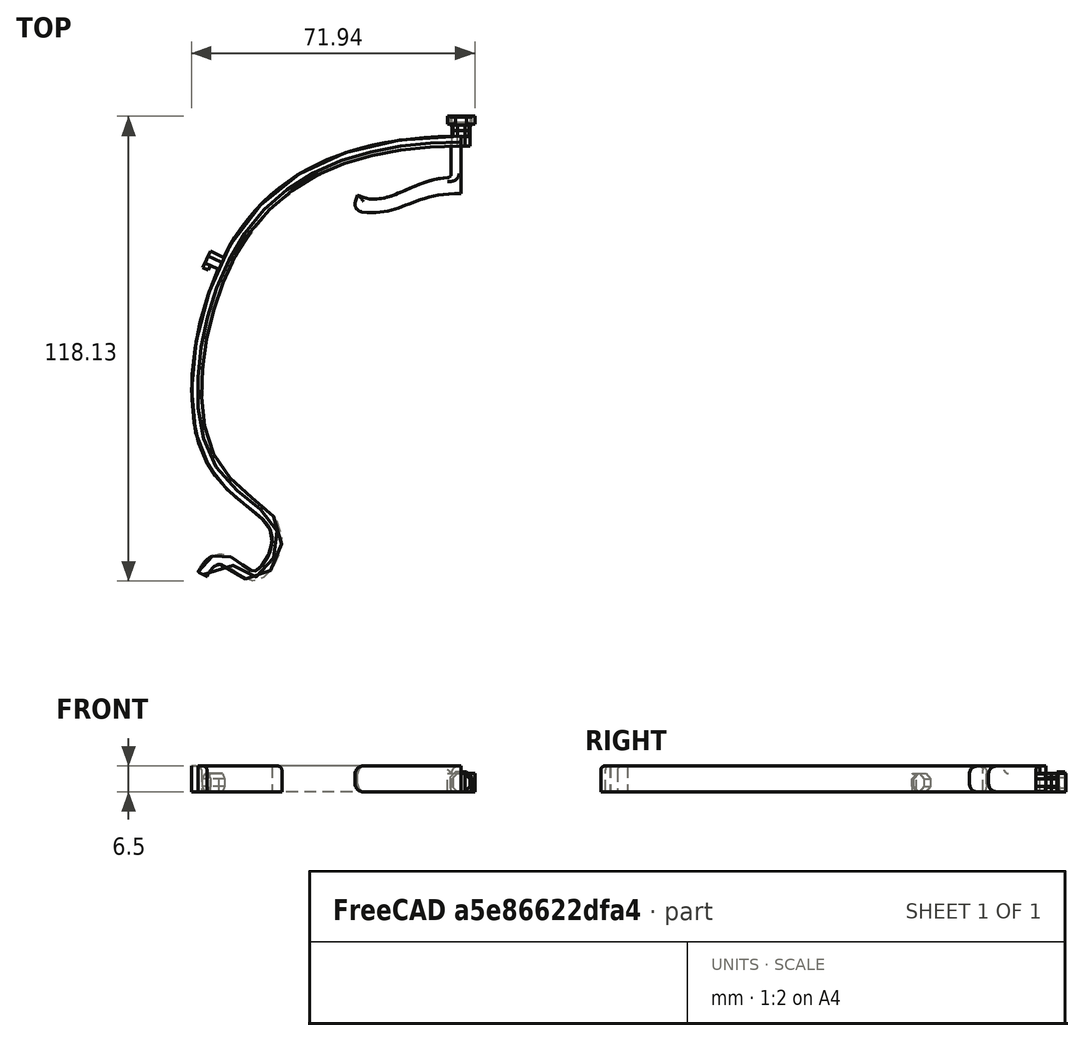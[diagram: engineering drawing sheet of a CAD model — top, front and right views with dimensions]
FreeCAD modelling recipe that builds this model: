
FCSTD DOCUMENT  (FreeCAD 0.18R16146 (Git))
Label: frame-001-03
License: All rights reserved
LicenseURL: http://ja.wikipedia.org/wiki/%E8%91%97%E4%BD%9C%E6%A8%A9%E8%A1%A8%E7%A4%BA
objects: Sketcher::SketchObject×5, Part::Extrusion×5, Part::Box×3, Part::Cut×2, Part::Fillet×2, Part::Compound×2, Mesh::Feature×1, Part::Sweep×1, Part::Mirroring×1, Part::MultiCommon×1
note: 22 computed .brp shape members not serialized (recipe doc carries the construction recipe); baked Part::Feature solids carry a one-line shape summary decoded from their .brp

FEATURE [Sketcher::SketchObject] Sketch  label="Sketch_FrameShape"
  sketch-geometry (15):
    g0-g7: Circle [constr] x8 (B-spline internal-alignment scaffolding for g8; pole/knot coordinates omitted)
    g8: BSplineCurve PolesCount=8 KnotsCount=6 Degree=3 IsPeriodic=0
    g9-g14: GeomPoint [constr] x6 (B-spline internal-alignment scaffolding for g8; pole/knot coordinates omitted)
  constraints (6):
    c: Radius(g0) = 6
    c: Equal(g0, g1-g6) x6
    c: InternalAlignment(g0-g7 -> g8) x8
    c: InternalAlignment(g9-g14 -> g8) x6
    c: Horizontal(g1,g8)
    c: Coincident(g-1,g8)
FEATURE [Sketcher::SketchObject] Sketch001
  Placement = pos=(0,0,0) rot=(0.57735,0.57735,0.57735;2.0944rad)
  sketch-geometry (4):
    g0: LineSegment StartX=0 StartY=6.5 StartZ=0 EndX=2.5 EndY=6.5 EndZ=0
    g1: LineSegment StartX=2.5 StartY=6.5 StartZ=0 EndX=2.5 EndY=0 EndZ=0
    g2: LineSegment StartX=2.5 StartY=0 StartZ=0 EndX=0 EndY=0 EndZ=0
    g3: LineSegment StartX=0 StartY=0 StartZ=0 EndX=0 EndY=6.5 EndZ=0
  constraints (12):
    c: Coincident(g0,g1)
    c: Coincident(g1,g2)
    c: Coincident(g2,g3)
    c: Coincident(g3,g0)
    c: Horizontal(g0)
    c: Horizontal(g2)
    c: Vertical(g1)
    c: Vertical(g3)
    c: DistanceX(g0,g0) = 2.5
    c: DistanceY(g1,g0) = 6.5
    c: DistanceX(g-1,g2) = 0
    c: PointOnObject(g2,g-1)
FEATURE [Mesh::Feature] cd43cbcc_75a4_11ea_893f_42010a00001e_UM3E_Visor_frame_EUROPE_ISO838_v3  label="cd43cbcc-75a4-11ea-893f-42010a00001e_UM3E_Visor_frame_EUROPE_ISO838_v3"
  Placement = pos=(0,-59,0) rot=(0,0,1;0rad)
FEATURE [Sketcher::SketchObject] Sketch002  label="OctPinSketch"
  Placement = pos=(0,0,0) rot=(1,0,0;1.5708rad)
  sketch-geometry (9):
    g0: LineSegment StartX=2.3097 StartY=1.35299 StartZ=0 EndX=2.3097 EndY=3.26641 EndZ=0
    g1: LineSegment StartX=2.3097 StartY=3.26641 StartZ=0 EndX=0.956709 EndY=4.6194 EndZ=0
    g2: LineSegment StartX=0.956709 StartY=4.6194 StartZ=0 EndX=-0.956709 EndY=4.6194 EndZ=0
    g3: LineSegment StartX=-0.956709 StartY=4.6194 StartZ=0 EndX=-2.3097 EndY=3.26641 EndZ=0
    g4: LineSegment StartX=-2.3097 StartY=3.26641 StartZ=0 EndX=-2.3097 EndY=1.35299 EndZ=0
    g5: LineSegment StartX=-2.3097 StartY=1.35299 StartZ=0 EndX=-0.956709 EndY=0 EndZ=0
    g6: LineSegment StartX=-0.956709 StartY=0 StartZ=0 EndX=0.956709 EndY=0 EndZ=0
    g7: LineSegment StartX=0.956709 StartY=0 StartZ=0 EndX=2.3097 EndY=1.35299 EndZ=0
    g8: Circle [constr] CenterX=0 CenterY=2.3097 CenterZ=0 NormalX=0 NormalY=0 NormalZ=1 AngleXU=0 Radius=2.5
  constraints (21):
    c: Coincident(g0,g1)
    c: Coincident(g1,g2)
    c: Coincident(g2,g3)
    c: Coincident(g3,g4)
    c: Coincident(g4,g5)
    c: Coincident(g5,g6)
    c: Coincident(g6,g7)
    c: Coincident(g7,g0)
    c: Equal(g0, g1-g7) x7
    c: PointOnObject(g0,g8)
    c: PointOnObject(g1,g8)
    c: PointOnObject(g2,g8)
    c: PointOnObject(g3,g8)
    c: PointOnObject(g4,g8)
    c: PointOnObject(g5,g8)
    c: PointOnObject(g6,g8)
    c: PointOnObject(g7,g8)
    c: Distance(g0,g8) = 2.5
    c: Horizontal(g6)
    c: PointOnObject(g8,g-2)
    c: PointOnObject(g6,g-1)
FEATURE [Part::Extrusion] Extrude002  label="OctPin"
  Base = -> Sketch002
  Dir = (0,-1,0)
  DirMode = 2
  FaceMakerClass = Part::FaceMakerBullseye
  LengthFwd = -6
  LengthRev = 0
  Solid = true
  Symmetric = false
FEATURE [Part::Extrusion] Extrude003  label="OctPinFront"
  Base = -> Sketch002
  Dir = (0,-1,2e-16)
  DirMode = 2
  FaceMakerClass = Part::FaceMakerBullseye
  LengthFwd = -3
  LengthRev = 0
  Placement = pos=(0,3,0) rot=(0,0,1;0rad)
  Solid = true
  Symmetric = false
FEATURE [Part::Extrusion] Extrude004  label="OctPin_WNotch_column"
  Base = -> Sketch002
  Dir = (0,-1,2e-16)
  DirMode = 2
  FaceMakerClass = Part::FaceMakerBullseye
  LengthFwd = -4
  LengthRev = 0
  Solid = true
  Symmetric = false
FEATURE [Part::Box] Box008  label="立方体008"
  AttacherType = Attacher::AttachEngine3D
  Height = 6
  Length = 2
  Placement = pos=(1,0,-0.5) rot=(0,0,1;0rad)
  Width = 2.5
FEATURE [Part::Cut] Cut  label="OctPin_WNotch"
  Base = -> Extrude004
  Tool = -> Box008
FEATURE [Part::Cut] Cut001  label="OctPin_WNotchR"
  Base = -> Extrude004
  Placement = pos=(61,-30.51,0) rot=(0,0,-1;1.13446rad)
  Tool = -> Box008
FEATURE [Sketcher::SketchObject] Sketch003
  sketch-geometry (18):
    g0: LineSegment StartX=0 StartY=1 StartZ=0 EndX=0 EndY=-12 EndZ=0
    g1: LineSegment StartX=2.5 StartY=-8 StartZ=0 EndX=2.5 EndY=1 EndZ=0
    g2: LineSegment StartX=2.5 StartY=1 StartZ=0 EndX=0 EndY=1 EndZ=0
    g3: LineSegment StartX=26.2521 StartY=-12.5 StartZ=0 EndX=27.6498 EndY=-16.2478 EndZ=0
    g4-g7: Circle [constr] x4 (B-spline internal-alignment scaffolding for g8; pole/knot coordinates omitted)
    g8: BSplineCurve PolesCount=4 KnotsCount=2 Degree=3 IsPeriodic=0
    g9: GeomPoint [constr] X=2.5 Y=-8 Z=0
    g10: GeomPoint [constr] X=26.2521 Y=-12.5 Z=0
    g11-g14: Circle [constr] x4 (B-spline internal-alignment scaffolding for g15; pole/knot coordinates omitted)
    g15: BSplineCurve PolesCount=4 KnotsCount=2 Degree=3 IsPeriodic=0
    g16: GeomPoint [constr] X=0 Y=-12 Z=0
    g17: GeomPoint [constr] X=27.6498 Y=-16.2478 Z=0
  constraints (32):
    c: PointOnObject(g0,g-2)
    c: Vertical(g0)
    c: Vertical(g1)
    c: Coincident(g1,g2)
    c: Coincident(g2,g0)
    c: DistanceX(g0,g1) = 2.5
    c: Horizontal(g2)
    c: DistanceY(g-1,g0) = 1
    c: DistanceY(g3,g1) = 4.5
    c: DistanceY(g0,g1) = 4
    c: DistanceY(g0,g-1) = 12
    c: Coincident(g8,g1)
    c: Radius(g4) = 2
    c: Equal(g4,g5)
    c: Equal(g4,g6)
    c: Equal(g4,g7)
    c: Coincident(g8,g3)
    c: InternalAlignment(g4-g7 -> g8) x4
    c: InternalAlignment(g9,g8)
    c: InternalAlignment(g10,g8)
    c: Coincident(g15,g0)
    c: Radius(g11) = 2
    c: Equal(g11,g12)
    c: Equal(g11,g13)
    c: Equal(g11,g14)
    c: Coincident(g15,g3)
    c: InternalAlignment(g11-g14 -> g15) x4
    c: InternalAlignment(g16,g15)
    c: InternalAlignment(g17,g15)
    c: Distance(g3,g3) = 4
    c: Horizontal(g0,g12)
    c: Horizontal(g5,g1)
FEATURE [Part::Extrusion] Extrude
  Base = -> Sketch003
  Dir = (0,0,1)
  DirMode = 2
  FaceMakerClass = Part::FaceMakerBullseye
  LengthFwd = 6.5
  LengthRev = 0
  Solid = true
  Symmetric = false
FEATURE [Part::Fillet] Fillet  label="AGOATE_R"
  Base = -> Extrude
  Edges = 8 edges: [Edge1 r=1,Edge4 r=2,Edge11 r=2,Edge12 r=2,Edge13 r=2,Edge15 r=2,Edge16 r=2,Edge18 r=1]
FEATURE [Part::Sweep] Sweep  label="Sweep_RightFrame"
  Frenet = false
  Sections = -> [Sketch001]
  Solid = true
  Spine = -> Sketch [Edge1]
  Transition = 1
FEATURE [Part::Fillet] Fillet001  label="Fillet_Sweep_RightFrame"
  Base = -> Sweep
  Edges = 1 edges r=1: [Edge1]
FEATURE [Part::Compound] Compound  label="RightSide"
  Links = -> [Cut001,Fillet,Fillet001]
FEATURE [Part::Mirroring] Part__Mirroring001  label="LeftSide (Mirrored)"
  Base = (2.38419e-07,-54.0124,3.5)
  Normal = (1,0,-1.19209e-07)
  Source = -> Compound
FEATURE [Part::Box] Box  label="立方体"
  AttacherType = Attacher::AttachEngine3D
  Height = 10
  Length = 4
  Placement = pos=(-2,2.8,0) rot=(0,0,1;0rad)
  Width = 4
FEATURE [Part::Box] Box010  label="立方体010"
  AttacherType = Attacher::AttachEngine3D
  Height = 4.7
  Length = 7
  Placement = pos=(-3.5,5.6,0) rot=(0,0,1;0rad)
  Width = 2
FEATURE [Part::MultiCommon] Common  label="前ダボ柱"
  Shapes = -> [Extrude003,Box]
FEATURE [Sketcher::SketchObject] Sketch004
  MapMode = 5
  Placement = pos=(0,6,0) rot=(0,0.707107,0.707107;3.14159rad)
  Support = -> [Common]
  sketch-geometry (8):
    g0: LineSegment StartX=-2.34451 StartY=0 StartZ=0 EndX=-2.75 EndY=1.00428 EndZ=0
    g1: LineSegment StartX=-2.75 StartY=1.00428 StartZ=0 EndX=-2.75 EndY=3.6504 EndZ=0
    g2: LineSegment StartX=-2.75 StartY=3.6504 StartZ=0 EndX=-1.4004 EndY=5 EndZ=0
    g3: LineSegment StartX=-1.4004 StartY=5 StartZ=0 EndX=1.4004 EndY=5 EndZ=0
    g4: LineSegment StartX=1.4004 StartY=5 StartZ=0 EndX=2.75 EndY=3.6504 EndZ=0
    g5: LineSegment StartX=2.75 StartY=3.6504 StartZ=0 EndX=2.75 EndY=1.00428 EndZ=0
    g6: LineSegment StartX=2.75 StartY=1.00428 StartZ=0 EndX=2.34451 EndY=0 EndZ=0
    g7: LineSegment StartX=2.34451 StartY=0 StartZ=0 EndX=-2.34451 EndY=0 EndZ=0
  constraints (17):
    c: Coincident(g0,g1)
    c: Coincident(g1,g2)
    c: Coincident(g2,g3)
    c: Coincident(g3,g4)
    c: Coincident(g4,g5)
    c: Coincident(g5,g6)
    c: Coincident(g6,g7)
    c: Coincident(g7,g0)
    c: Vertical(g1)
    c: Symmetric(g0,g6,g-2)
    c: Symmetric(g0,g5,g-2)
    c: Symmetric(g1,g4,g-2)
    c: Symmetric(g2,g3,g-2)
    c: PointOnObject(g6,g-1)
    c: DistanceY(g6,g3) = 5
    c: DistanceX(g0,g5) = 5.5
    c: Angle(g5,g4,g4) = 0.785398
FEATURE [Part::Extrusion] Extrude005  label="前ダボトメ"
  Base = -> Sketch004
  Dir = (0,1,-2e-16)
  DirMode = 2
  FaceMakerClass = Part::FaceMakerBullseye
  LengthFwd = 2
  LengthRev = 0
  Solid = true
  Symmetric = false
FEATURE [Part::Compound] Compound001  label="前ダボ"
  Links = -> [Common,Extrude005]
  Placement = pos=(0,-0.6,0) rot=(0,0,1;0rad)
